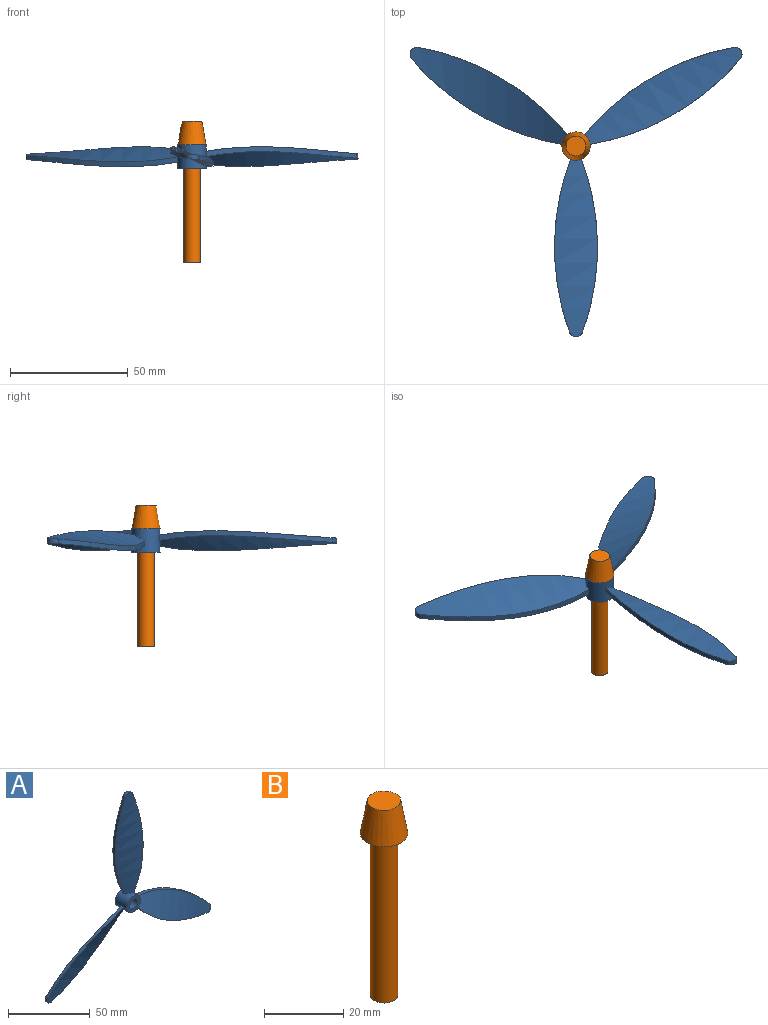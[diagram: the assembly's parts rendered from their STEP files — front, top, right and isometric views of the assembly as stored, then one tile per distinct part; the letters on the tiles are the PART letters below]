
ASSEMBLY  parts=2 mates=1
PART A: 19 faces, bbox 188.2x16.7x163 mm
  f0: bspline ~100x30mm, area 1083.3mm2, adj f1,f2,f4,f5
  f1: cylinder r=106mm len=73.47mm, axis (0,1,0), area 154.2mm2, adj f0,f3,f4,f5
  f2: cylinder r=106mm len=73.47mm, axis (0,1,0), area 154.2mm2, adj f0,f3,f4,f5
  f3: bspline ~100x30mm, area 1083.3mm2, adj f1,f2,f4,f5
  f4: cylinder r=3mm len=5.64mm, axis (0,1,0), area 14.4mm2, adj f0,f1,f2,f3
  f5: cylinder r=6mm len=12mm, axis (0,1,0), area 345.3mm2, adj f0,f1,f2,f3,f6,f7,f8,f9
  f6: plane 12x12mm, normal (0,-1,0), area 74.6mm2, adj f5,f18
  f7: plane 12x12mm, normal (0,1,0), area 74.6mm2, adj f5,f18
  f8: bspline ~100.85x73.81mm, area 1083.3mm2, adj f5,f9,f10,f12
  f9: cylinder r=106mm len=63.35mm, axis (0,1,0), area 154.2mm2, adj f5,f8,f11,f12
  f10: cylinder r=106mm len=63.9mm, axis (0,1,0), area 154.2mm2, adj f5,f8,f11,f12
  f11: bspline ~100.35x74.67mm, area 1083.3mm2, adj f5,f9,f10,f12
  f12: cylinder r=3mm len=4.93mm, axis (0,1,0), area 14.4mm2, adj f8,f9,f10,f11
  f13: bspline ~100.35x74.67mm, area 1083.3mm2, adj f5,f14,f15,f17
  f14: cylinder r=106mm len=63.9mm, axis (0,1,0), area 154.2mm2, adj f5,f13,f16,f17
  f15: cylinder r=106mm len=63.35mm, axis (0,1,0), area 154.2mm2, adj f5,f13,f16,f17
  f16: bspline ~100.85x73.81mm, area 1083.3mm2, adj f5,f14,f15,f17
  f17: cylinder r=3mm len=4.93mm, axis (0,1,0), area 14.4mm2, adj f13,f14,f15,f16
  f18: cylinder r=3.5mm len=10mm, axis (0,-1,0), area 219.9mm2, adj f6,f7
PART B: 5 faces, bbox 12x12x60 mm
  f0: cylinder r=3.5mm len=50mm, axis (0,0,-1), area 1099.6mm2, adj f1,f4
  f1: plane 7x7mm, normal (0,0,-1), area 38.5mm2, adj f0
  f2: cone r=6mm half-angle=10deg, axis (0,0,-1), area 326.6mm2, adj f3,f4
  f3: plane 8.47x8.47mm, normal (0,0,1), area 56.4mm2, adj f2
  f4: plane 12x12mm, normal (0,0,-1), area 74.6mm2, adj f0,f2
PLACE A rot(axis=(1,0,0),90deg) t=(-59.37,-25.29,28.48)mm
PLACE B t=(-59.37,-25.29,-16.52)mm fixed
MATE revolute A.f5 <-> B.f2  axis (0,0,-1) through (-59.37,-25.29,23.48)mm
